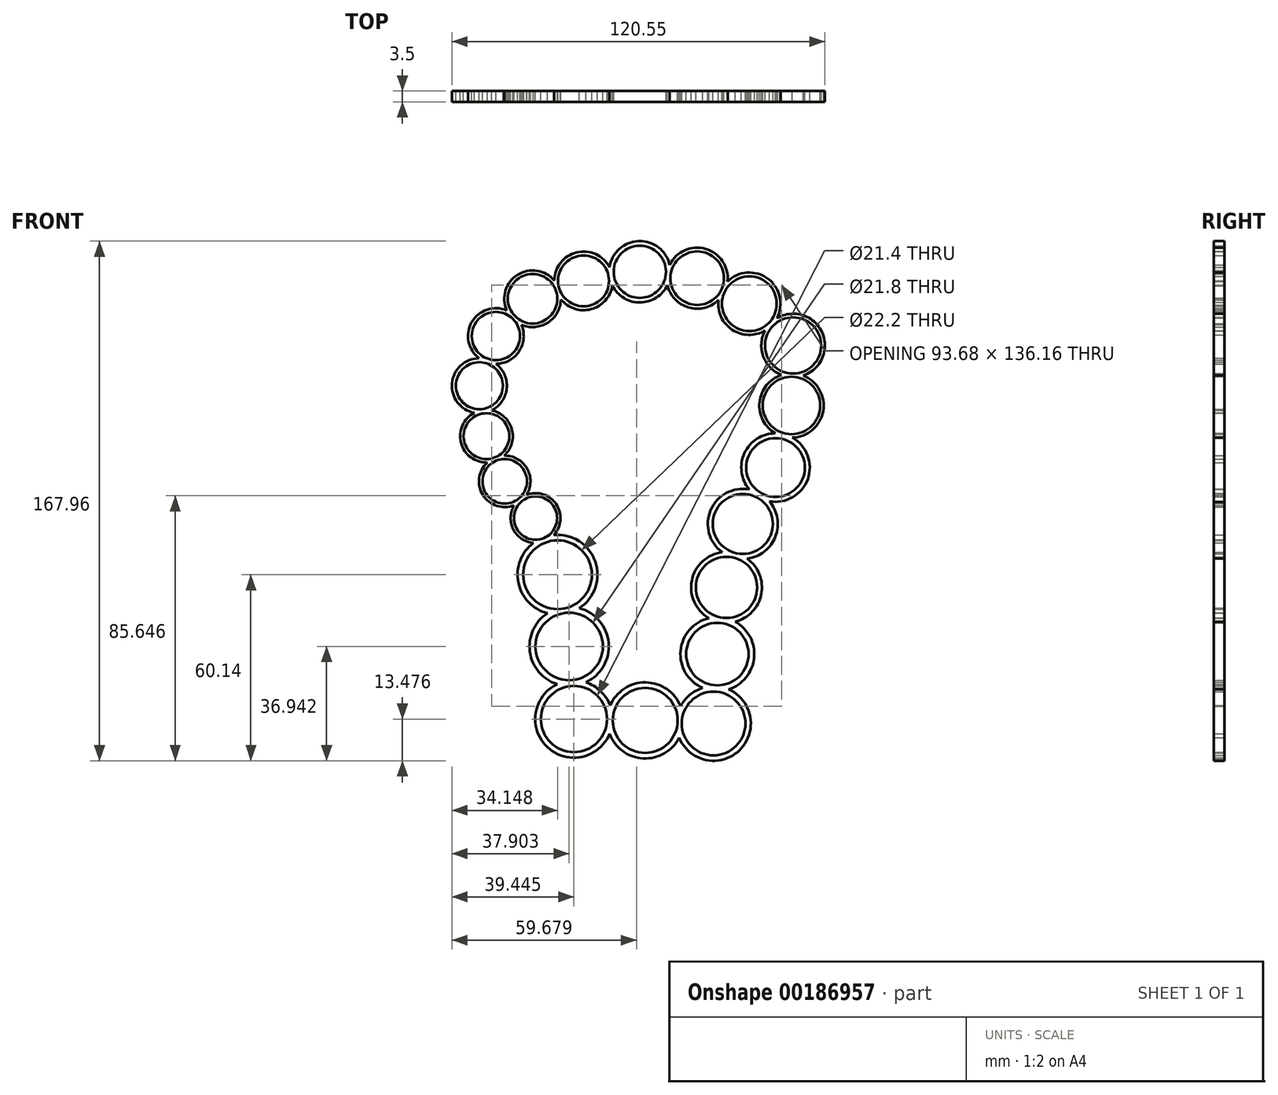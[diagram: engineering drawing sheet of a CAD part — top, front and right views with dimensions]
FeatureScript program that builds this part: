
annotation { "Feature Type Name" : "Feature", "Feature Type Description" : "" }
export const myFeature = defineFeature(function(context is Context, id is Id, definition is map)
    precondition{}
    {
        {
            var Q0;
            Q0=qCreatedBy(makeId("Front.planeOp"),FACE);
            var sketch = newSketch(context, id + "F0", { "sketchPlane" : qUnion([Q0])});
            skCircle(sketch, "E0", {"center": v(-45.31, 3.88) * mm, "radius": 7.2 * mm});
            skCircle(sketch, "E1", {"center": v(-51.2, 18.48) * mm, "radius": 7.4 * mm});
            skCircle(sketch, "E2", {"center": v(-53.5, 34.77) * mm, "radius": 7.6 * mm});
            skCircle(sketch, "E3", {"center": v(-48.16, 50.85) * mm, "radius": 7.8 * mm});
            skCircle(sketch, "E4", {"center": v(-36.3, 62.9) * mm, "radius": 8 * mm});
            skCircle(sketch, "E5", {"center": v(-1.64, 71.6) * mm, "radius": 8.45 * mm});
            skCircle(sketch, "E6", {"center": v(33.76, 61.3) * mm, "radius": 8.85 * mm});
            skCircle(sketch, "E7", {"center": v(16.9, 69.55) * mm, "radius": 8.65 * mm});
            skCircle(sketch, "E8", {"center": v(42.23, 8.34) * mm, "radius": 9.5 * mm});
            skCircle(sketch, "E9", {"center": v(-22.93, -72.95) * mm, "radius": 10.7 * mm});
            skCircle(sketch, "E10", {"center": v(0.1, -73.4) * mm, "radius": 10.5 * mm});
            skCircle(sketch, "E11", {"center": v(22.22, -74.4) * mm, "radius": 10.3 * mm});
            skCircle(sketch, "E12", {"center": v(23.43, -51.97) * mm, "radius": 10.1 * mm});
            skCircle(sketch, "E13", {"center": v(-24.48, -49.49) * mm, "radius": 10.9 * mm});
            skCircle(sketch, "E14", {"center": v(31.66, -9.9) * mm, "radius": 9.7 * mm});
            skCircle(sketch, "E15", {"center": v(-19.82, 68.67) * mm, "radius": 8.22 * mm});
            skCircle(sketch, "E16", {"center": v(47.9, 47.8) * mm, "radius": 9.1 * mm});
            skCircle(sketch, "E17", {"center": v(-35.35, -7.99) * mm, "radius": 7 * mm});
            skCircle(sketch, "E18", {"center": v(47.39, 28.39) * mm, "radius": 9.3 * mm});
            skCircle(sketch, "E19", {"center": v(26.4, -30.4) * mm, "radius": 9.9 * mm});
            skCircle(sketch, "E20", {"center": v(-28.23, -26.29) * mm, "radius": 11.1 * mm});
            skArc(sketch, "E21", {"start": v(-38.22, -0.47) * mm, "mid": v(-38.1, 8.02) * mm, "end": v(-45.49, 12.2) * mm});
            skArc(sketch, "E22", {"start": v(-42.26, -3.86) * mm, "mid": v(-43.31, -6.81) * mm, "end": v(-43.16, -9.94) * mm});
            skArc(sketch, "E23", {"start": v(-45.49, 12.2) * mm, "mid": v(-43.01, 20.75) * mm, "end": v(-49.54, 26.82) * mm});
            skArc(sketch, "E24", {"start": v(-50.96, 9.98) * mm, "mid": v(-52.36, -0.55) * mm, "end": v(-42.26, -3.86) * mm});
            skArc(sketch, "E25", {"start": v(-29.42, -13.44) * mm, "mid": v(-28.68, -3.47) * mm, "end": v(-38.22, -0.47) * mm});
            skArc(sketch, "E26", {"start": v(-36.03, -16) * mm, "mid": v(-40.89, -28.8) * mm, "end": v(-31.5, -38.77) * mm});
            skArc(sketch, "E27", {"start": v(-49.54, 26.82) * mm, "mid": v(-44.65, 33.95) * mm, "end": v(-48.14, 41.86) * mm});
            skArc(sketch, "E28", {"start": v(-55.1, 26.04) * mm, "mid": v(-59.44, 16.36) * mm, "end": v(-50.96, 9.98) * mm});
            skLineSegment(sketch, "E29", {"start": v(-48.14, 41.86) * mm, "end": v(-48.14, 41.86) * mm});
            skLineSegment(sketch, "E30", {"start": v(-53.55, 43.65) * mm, "end": v(-53.55, 43.65) * mm});
            skArc(sketch, "E31", {"start": v(-48.14, 41.86) * mm, "mid": v(-40.62, 45.95) * mm, "end": v(-39.93, 54.49) * mm});
            skArc(sketch, "E32", {"start": v(-44.65, 59.13) * mm, "mid": v(-55.95, 55.33) * mm, "end": v(-53.55, 43.65) * mm});
            skArc(sketch, "E33", {"start": v(-39.93, 54.49) * mm, "mid": v(-31.36, 55.18) * mm, "end": v(-27.15, 62.68) * mm});
            skArc(sketch, "E34", {"start": v(-53.55, 43.65) * mm, "mid": v(-62.34, 35.55) * mm, "end": v(-55.1, 26.04) * mm});
            skArc(sketch, "E35", {"start": v(-29.29, 68.77) * mm, "mid": v(-41.17, 70.65) * mm, "end": v(-44.65, 59.13) * mm});
            skArc(sketch, "E36", {"start": v(-27.15, 62.68) * mm, "mid": v(-17.39, 59.52) * mm, "end": v(-10.48, 67.12) * mm});
            skArc(sketch, "E37", {"start": v(-11.45, 73.09) * mm, "mid": v(-22.05, 77.87) * mm, "end": v(-29.29, 68.77) * mm});
            skArc(sketch, "E38", {"start": v(-10.48, 67.12) * mm, "mid": v(-1.54, 61.69) * mm, "end": v(7.3, 67.3) * mm});
            skArc(sketch, "E39", {"start": v(7.3, 67.3) * mm, "mid": v(14.11, 60.08) * mm, "end": v(23.75, 62.45) * mm});
            skArc(sketch, "E40", {"start": v(8.03, 73.85) * mm, "mid": v(-2.03, 81.52) * mm, "end": v(-11.45, 73.09) * mm});
            skArc(sketch, "E41", {"start": v(26.71, 68.5) * mm, "mid": v(19.62, 79.03) * mm, "end": v(8.03, 73.85) * mm});
            skArc(sketch, "E42", {"start": v(23.75, 62.45) * mm, "mid": v(28.26, 52.86) * mm, "end": v(38.84, 52.6) * mm});
            skArc(sketch, "E43", {"start": v(42.68, 56.62) * mm, "mid": v(39.77, 69.38) * mm, "end": v(26.71, 68.5) * mm});
            skArc(sketch, "E44", {"start": v(38.84, 52.6) * mm, "mid": v(38.28, 44.24) * mm, "end": v(44.14, 38.24) * mm});
            skArc(sketch, "E45", {"start": v(51.16, 38.06) * mm, "mid": v(57.24, 52.05) * mm, "end": v(42.68, 56.62) * mm});
            skArc(sketch, "E46", {"start": v(44.14, 38.24) * mm, "mid": v(37.06, 29.45) * mm, "end": v(42.2, 19.4) * mm});
            skArc(sketch, "E47", {"start": v(47.6, 18.01) * mm, "mid": v(57.6, 26.57) * mm, "end": v(51.16, 38.06) * mm});
            skArc(sketch, "E48", {"start": v(42.2, 19.4) * mm, "mid": v(32.2, 13) * mm, "end": v(33.75, 1.22) * mm});
            skArc(sketch, "E49", {"start": v(33.75, 1.22) * mm, "mid": v(21.26, -5.42) * mm, "end": v(25.02, -19.06) * mm});
            skArc(sketch, "E50", {"start": v(40.27, -2.56) * mm, "mid": v(52.65, 4.62) * mm, "end": v(47.6, 18.01) * mm});
            skArc(sketch, "E51", {"start": v(33.06, -21.12) * mm, "mid": v(42.2, -13.99) * mm, "end": v(40.27, -2.56) * mm});
            skArc(sketch, "E52", {"start": v(25.02, -19.06) * mm, "mid": v(15.18, -28.15) * mm, "end": v(20.73, -40.34) * mm});
            skArc(sketch, "E53", {"start": v(-31.5, -38.77) * mm, "mid": v(-37.17, -51.23) * mm, "end": v(-28.36, -61.7) * mm});
            skArc(sketch, "E54", {"start": v(-21.2, -37.1) * mm, "mid": v(-16.04, -22.05) * mm, "end": v(-29.42, -13.44) * mm});
            skArc(sketch, "E55", {"start": v(20.73, -40.34) * mm, "mid": v(11.54, -50.87) * mm, "end": v(18.64, -62.9) * mm});
            skArc(sketch, "E56", {"start": v(29.16, -41.5) * mm, "mid": v(37.62, -32.55) * mm, "end": v(33.06, -21.12) * mm});
            skArc(sketch, "E57", {"start": v(18.64, -62.9) * mm, "mid": v(14.49, -65.17) * mm, "end": v(11.53, -68.86) * mm});
            skArc(sketch, "E58", {"start": v(27.01, -63.36) * mm, "mid": v(35.32, -53.14) * mm, "end": v(29.16, -41.5) * mm});
            skArc(sketch, "E59", {"start": v(-19.03, -61.08) * mm, "mid": v(-11.72, -48.34) * mm, "end": v(-21.2, -37.1) * mm});
            skArc(sketch, "E60", {"start": v(-28.36, -61.7) * mm, "mid": v(-31.52, -82.03) * mm, "end": v(-11.4, -77.75) * mm});
            skArc(sketch, "E61", {"start": v(-11.22, -68.6) * mm, "mid": v(-14.27, -63.95) * mm, "end": v(-19.03, -61.08) * mm});
            skArc(sketch, "E62", {"start": v(-11.4, -77.75) * mm, "mid": v(-0.55, -85.68) * mm, "end": v(11.08, -78.95) * mm});
            skArc(sketch, "E63", {"start": v(11.53, -68.86) * mm, "mid": v(0.24, -61.1) * mm, "end": v(-11.22, -68.6) * mm});
            skArc(sketch, "E64", {"start": v(11.08, -78.95) * mm, "mid": v(30.63, -83) * mm, "end": v(27.01, -63.36) * mm});
            skPoint(sketch, "E65.orphan", {"position": v(-43.16, -10.27) * mm});
            skArc(sketch, "E66", {"start": v(-43.16, -9.94) * mm, "mid": v(-43.11, -10.1) * mm, "end": v(-43.07, -10.27) * mm});
            skArc(sketch, "E67", {"start": v(-43.07, -10.27) * mm, "mid": v(-40.43, -14.23) * mm, "end": v(-36.03, -16) * mm});
            skLineSegment(sketch, "E68", {"start": v(-57, -8.76) * mm, "end": v(-53.39, -8.76) * mm});
            skSolve(sketch);
        }
        {
            var Q0;
            Q0=makeQuery(id+"F0.imprint","IMPRINT",FACE,{"disambiguationData":[TD([[makeQuery(id+"F0.imprint","IMPRINT",EDGE,{"derivedFrom":sQuery(id+"F0.wireOp",EDGE,"E0")}),-1.0]])]});
            extrude(context, id + "F1", {"entities" : qUnion([Q0]), "depth" : 3.5 * mm});
        }
    });
